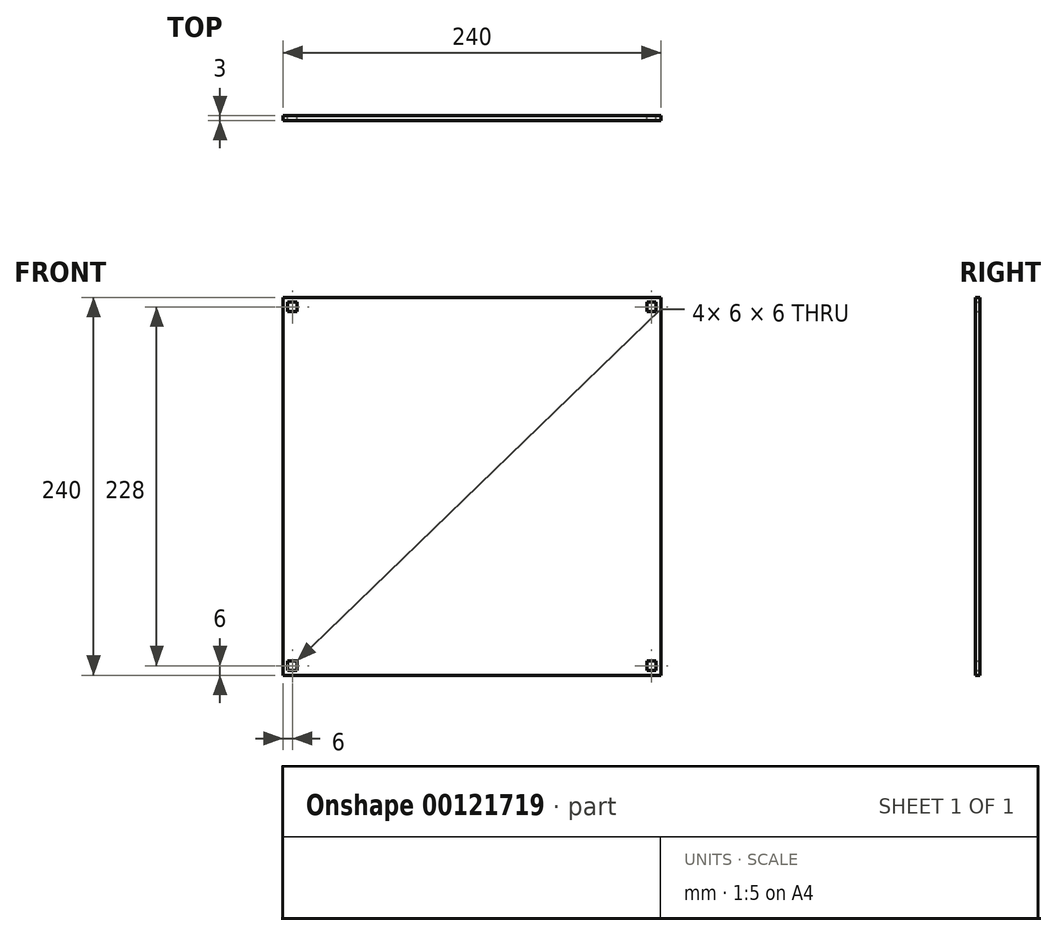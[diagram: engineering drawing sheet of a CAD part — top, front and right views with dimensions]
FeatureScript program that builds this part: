
annotation { "Feature Type Name" : "Feature", "Feature Type Description" : "" }
export const myFeature = defineFeature(function(context is Context, id is Id, definition is map)
    precondition{}
    {
        {
            assignVariable(context, id + "F0", {"name" : "thicknessWood", "anyValue" : 3});
        }
        {
            var Q0;
            Q0=qCreatedBy(makeId("Front.planeOp"),FACE);
            var sketch = newSketch(context, id + "F1", { "sketchPlane" : qUnion([Q0])});
            skLineSegment(sketch, "E0.bottom", {"start": v(0, 0) * mm, "end": v(240, 0) * mm});
            skLineSegment(sketch, "E0.top", {"start": v(0, 240) * mm, "end": v(240, 240) * mm});
            skLineSegment(sketch, "E0.left", {"start": v(0, 0) * mm, "end": v(0, 240) * mm});
            skLineSegment(sketch, "E0.right", {"start": v(240, 0) * mm, "end": v(240, 240) * mm});
            skLineSegment(sketch, "E1.bottom", {"start": v(9, 237) * mm, "end": v(3, 237) * mm});
            skLineSegment(sketch, "E1.top", {"start": v(9, 231) * mm, "end": v(3, 231) * mm});
            skLineSegment(sketch, "E1.left", {"start": v(9, 237) * mm, "end": v(9, 231) * mm});
            skLineSegment(sketch, "E1.right", {"start": v(3, 237) * mm, "end": v(3, 231) * mm});
            skLineSegment(sketch, "E2", {"start": v(120, 240) * mm, "end": v(120, 0) * mm, "construction": true});
            skLineSegment(sketch, "E3", {"start": v(0, 120) * mm, "end": v(240, 120) * mm, "construction": true});
            skSolve(sketch);
        }
        {
            var Q0;
            Q0=makeQuery(id+"F1.imprint","IMPRINT",FACE,{"disambiguationData":[TD([[makeQuery(id+"F1.imprint","IMPRINT",EDGE,{"derivedFrom":sQuery(id+"F1.wireOp",EDGE,"E0.bottom")}),1.0]])]});
            var Q1;
            Q1=makeQuery(id+"F1.imprint","IMPRINT",FACE,{"disambiguationData":[TD([[makeQuery(id+"F1.imprint","IMPRINT",EDGE,{"derivedFrom":sQuery(id+"F1.wireOp",EDGE,"E1.bottom")}),1.0]])]});
            var Q2;
            Q2=sQuery(id+"F1.wireOp",EDGE,"LAM1Qkwg-5DDv-CvPh-Ubu6-rHJoipJcaKlL.left");
            extrude(context, id + "F2", {"entities" : qUnion([Q0, Q1]), "surfaceEntities" : qUnion([Q2]), "depth" : (getVariable(context, 'thicknessWood')) * mm});
        }
        {
            var Q0;
            Q0=makeQuery(id+"F1.imprint","IMPRINT",FACE,{"disambiguationData":[TD([[makeQuery(id+"F1.imprint","IMPRINT",EDGE,{"derivedFrom":sQuery(id+"F1.wireOp",EDGE,"E1.bottom")}),1.0]])]});
            extrude(context, id + "F3", {"entities" : qUnion([Q0]), "operationType" : NewBodyOperationType.REMOVE, "depth" : 25 * mm});
        }
        {
            var Q0;
            Q0=makeQuery(id+"F2.opExtrude","SWEPT_FACE",FACE,{"disambiguationData":[OSD([sQuery(id+"F1.wireOp",EDGE,"E0.left")])]});
            var Q1;
            Q1=makeQuery(id+"F2.opExtrude","SWEPT_FACE",FACE,{"disambiguationData":[OSD([sQuery(id+"F1.wireOp",EDGE,"E0.right")])]});
            cPlane(context, id + "F4", {"entities" : qUnion([Q0, Q1]), "cplaneType" : CPlaneType.MID_PLANE, "offset" : 25 * mm, "width" : 150 * mm, "height" : 150 * mm});
        }
        {
            var Q0;
            Q0=makeQuery(id+"F2.opExtrude","SWEPT_BODY",BODY,{"disambiguationData":[OSD([sQuery(id+"F1.wireOp",EDGE,"E0.bottom"),sQuery(id+"F1.wireOp",EDGE,"E0.top"),sQuery(id+"F1.wireOp",EDGE,"E0.left"),sQuery(id+"F1.wireOp",EDGE,"E0.right"),sQuery(id+"F1.wireOp",EDGE,"LAM1Qkwg-5DDv-CvPh-Ubu6-rHJoipJcaKlL.bottom"),sQuery(id+"F1.wireOp",EDGE,"LAM1Qkwg-5DDv-CvPh-Ubu6-rHJoipJcaKlL.top"),sQuery(id+"F1.wireOp",EDGE,"LAM1Qkwg-5DDv-CvPh-Ubu6-rHJoipJcaKlL.left"),sQuery(id+"F1.wireOp",EDGE,"LAM1Qkwg-5DDv-CvPh-Ubu6-rHJoipJcaKlL.right")])]});
            var Q1;
            Q1=qCreatedBy(id+"F4.planeOp",FACE);
            mirror(context, id + "F5", {"operationType" : NewBodyOperationType.INTERSECT, "entities" : qUnion([Q0]), "mirrorPlane" : qUnion([Q1])});
        }
        {
            var Q0;
            Q0=makeQuery(id+"F2.opExtrude","SWEPT_FACE",FACE,{"disambiguationData":[OSD([sQuery(id+"F1.wireOp",EDGE,"E0.top")])]});
            var Q1;
            Q1=makeQuery(id+"F2.opExtrude","SWEPT_FACE",FACE,{"disambiguationData":[OSD([sQuery(id+"F1.wireOp",EDGE,"E0.bottom")])]});
            cPlane(context, id + "F6", {"entities" : qUnion([Q0, Q1]), "cplaneType" : CPlaneType.MID_PLANE, "offset" : 25 * mm, "width" : 150 * mm, "height" : 150 * mm});
        }
        {
            var Q0;
            Q0=makeQuery(id+"F2.opExtrude","SWEPT_BODY",BODY,{"disambiguationData":[OSD([sQuery(id+"F1.wireOp",EDGE,"E0.bottom"),sQuery(id+"F1.wireOp",EDGE,"E0.top"),sQuery(id+"F1.wireOp",EDGE,"E0.left"),sQuery(id+"F1.wireOp",EDGE,"E0.right"),sQuery(id+"F1.wireOp",EDGE,"LAM1Qkwg-5DDv-CvPh-Ubu6-rHJoipJcaKlL.bottom"),sQuery(id+"F1.wireOp",EDGE,"LAM1Qkwg-5DDv-CvPh-Ubu6-rHJoipJcaKlL.top"),sQuery(id+"F1.wireOp",EDGE,"LAM1Qkwg-5DDv-CvPh-Ubu6-rHJoipJcaKlL.left"),sQuery(id+"F1.wireOp",EDGE,"LAM1Qkwg-5DDv-CvPh-Ubu6-rHJoipJcaKlL.right")])]});
            var Q1;
            Q1=qCreatedBy(id+"F6.planeOp",FACE);
            mirror(context, id + "F7", {"operationType" : NewBodyOperationType.INTERSECT, "entities" : qUnion([Q0]), "mirrorPlane" : qUnion([Q1])});
        }
    });
